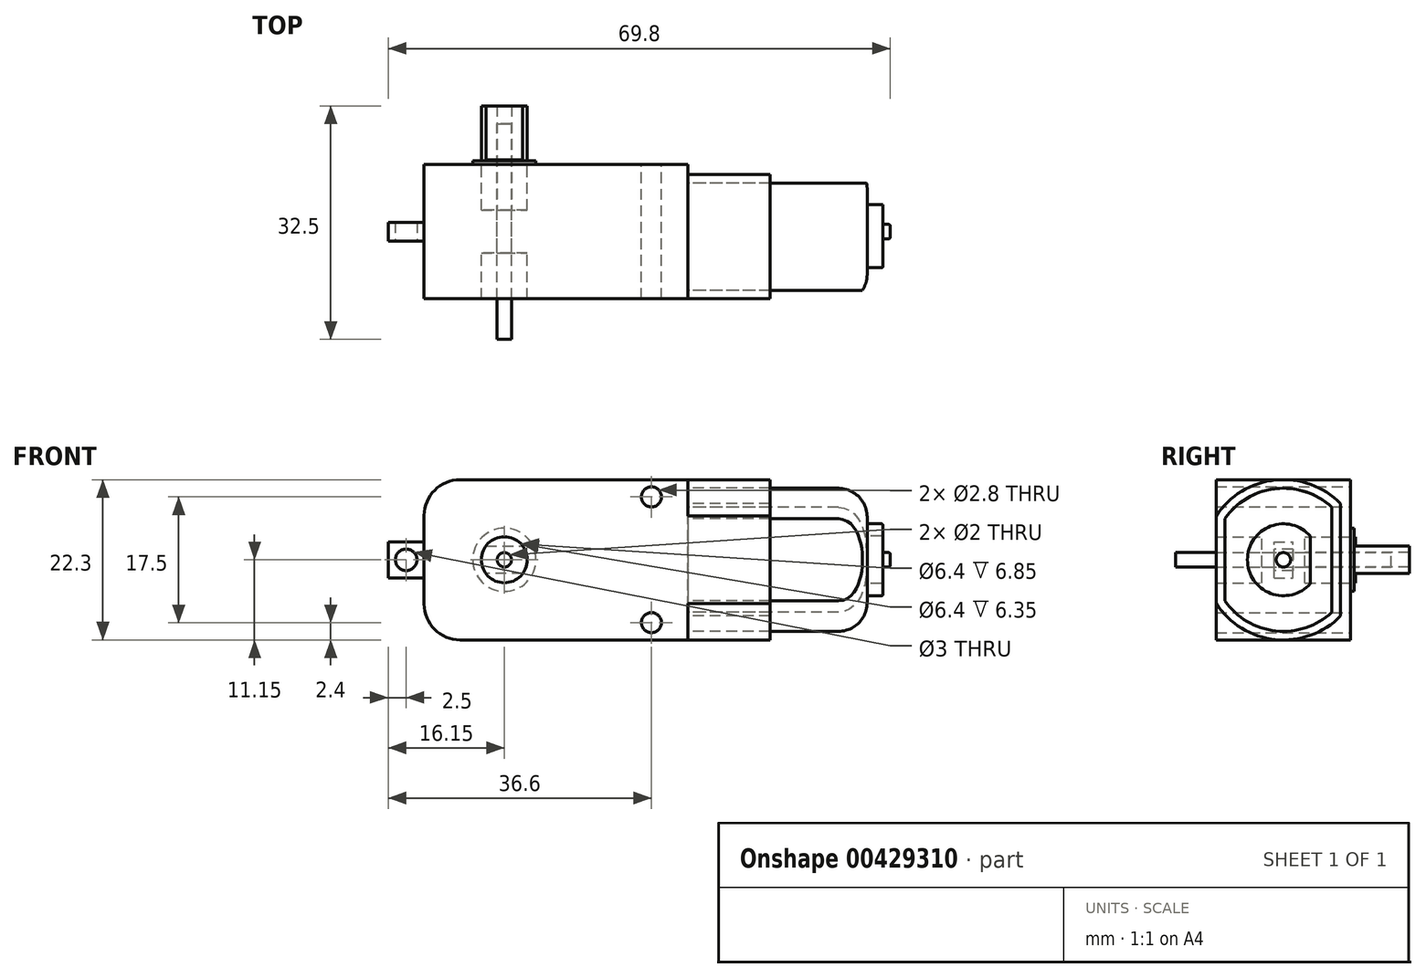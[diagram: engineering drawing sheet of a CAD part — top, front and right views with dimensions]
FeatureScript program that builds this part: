
annotation { "Feature Type Name" : "Feature", "Feature Type Description" : "" }
export const myFeature = defineFeature(function(context is Context, id is Id, definition is map)
    precondition{}
    {
        {
            var Q0;
            Q0=qCreatedBy(makeId("Front.planeOp"),FACE);
            var sketch = newSketch(context, id + "F0", { "sketchPlane" : qUnion([Q0])});
            skLineSegment(sketch, "E0.bottom", {"start": v(18.35, -11.15) * mm, "end": v(-13.35, -11.15) * mm});
            skLineSegment(sketch, "E0.top", {"start": v(18.35, 11.15) * mm, "end": v(-13.35, 11.15) * mm});
            skLineSegment(sketch, "E0.left", {"start": v(18.35, -11.15) * mm, "end": v(18.35, 11.15) * mm});
            skLineSegment(sketch, "E0.right", {"start": v(-18.35, -6.15) * mm, "end": v(-18.35, 6.15) * mm});
            skPoint(sketch, "E0.middle", {"position": v(0, 0) * mm});
            skPoint(sketch, "E1.visualSharp", {"position": v(-18.35, 11.15) * mm});
            skArc(sketch, "E1.filletArc", {"start": v(-13.35, 11.15) * mm, "mid": v(-16.89, 9.69) * mm, "end": v(-18.35, 6.15) * mm});
            skPoint(sketch, "E2.visualSharp", {"position": v(-18.35, -11.15) * mm});
            skArc(sketch, "E2.filletArc", {"start": v(-18.35, -6.15) * mm, "mid": v(-16.89, -9.69) * mm, "end": v(-13.35, -11.15) * mm});
            skLineSegment(sketch, "E3", {"start": v(-27.57, 10.15) * mm, "end": v(27, 10.15) * mm, "construction": true});
            skLineSegment(sketch, "E4", {"start": v(27, -10.15) * mm, "end": v(-33.16, -10.15) * mm, "construction": true});
            skLineSegment(sketch, "E5", {"start": v(14.65, 15.01) * mm, "end": v(14.65, -22.1) * mm, "construction": true});
            skCircle(sketch, "E6", {"center": v(13.25, 8.75) * mm, "radius": 1.4 * mm});
            skCircle(sketch, "E7.MirrorC", {"center": v(13.25, -8.75) * mm, "radius": 1.4 * mm});
            skCircle(sketch, "E8", {"center": v(-7.2, 0) * mm, "radius": 3.2 * mm});
            skCircle(sketch, "E9", {"center": v(-7.2, 0) * mm, "radius": 1 * mm});
            skSolve(sketch);
        }
        {
            var Q0;
            Q0=makeQuery(id+"F0.imprint","IMPRINT",FACE,{"disambiguationData":[TD([[makeQuery(id+"F0.imprint","IMPRINT",EDGE,{"derivedFrom":sQuery(id+"F0.wireOp",EDGE,"E0.bottom")}),-1.0]])]});
            extrude(context, id + "F1", {"entities" : qUnion([Q0]), "endBound" : BoundingType.SYMMETRIC, "depth" : (18.7) * mm});
        }
        {
            var Q0;
            Q0=makeQuery(id+"F1.opExtrude","SWEPT_FACE",FACE,{"disambiguationData":[OSD([sQuery(id+"F0.wireOp",EDGE,"E0.right")])]});
            var sketch = newSketch(context, id + "F2", { "sketchPlane" : qUnion([Q0])});
            skLineSegment(sketch, "E10.bottom", {"start": v(1.3, -2.5) * mm, "end": v(-1.3, -2.5) * mm});
            skLineSegment(sketch, "E10.top", {"start": v(1.3, 2.5) * mm, "end": v(-1.3, 2.5) * mm});
            skLineSegment(sketch, "E10.left", {"start": v(1.3, -2.5) * mm, "end": v(1.3, 2.5) * mm});
            skLineSegment(sketch, "E10.right", {"start": v(-1.3, -2.5) * mm, "end": v(-1.3, 2.5) * mm});
            skPoint(sketch, "E10.middle", {"position": v(0, 0) * mm});
            skSolve(sketch);
        }
        {
            var Q0;
            Q0=makeQuery(id+"F2.imprint","IMPRINT",FACE,{"disambiguationData":[TD([[makeQuery(id+"F2.imprint","IMPRINT",EDGE,{"derivedFrom":sQuery(id+"F2.wireOp",EDGE,"E10.bottom")}),-1.0]])]});
            extrude(context, id + "F3", {"entities" : qUnion([Q0]), "operationType" : NewBodyOperationType.ADD, "depth" : 5 * mm});
        }
        {
            var Q0;
            Q0=makeQuery(id+"F3.opExtrude","SWEPT_FACE",FACE,{"disambiguationData":[OSD([sQuery(id+"F2.wireOp",EDGE,"E10.left")])]});
            var sketch = newSketch(context, id + "F4", { "sketchPlane" : qUnion([Q0])});
            skLineSegment(sketch, "E11", {"start": v(-23.35, 0) * mm, "end": v(-18.35, 0) * mm, "construction": true});
            skCircle(sketch, "E12", {"center": v(-20.85, 0) * mm, "radius": 1.5 * mm});
            skSolve(sketch);
        }
        {
            var Q0;
            Q0=makeQuery(id+"F4.imprint","IMPRINT",FACE,{"disambiguationData":[TD([[makeQuery(id+"F4.imprint","IMPRINT",EDGE,{"derivedFrom":sQuery(id+"F4.wireOp",EDGE,"E12")}),1.0]])]});
            extrude(context, id + "F5", {"entities" : qUnion([Q0]), "operationType" : NewBodyOperationType.REMOVE, "endBound" : BoundingType.THROUGH_ALL, "oppositeDirection" : true, "depth" : 25 * mm});
        }
        {
            var Q0;
            Q0=makeQuery(id+"F1.opExtrude","SWEPT_FACE",FACE,{"disambiguationData":[OSD([sQuery(id+"F0.wireOp",EDGE,"E0.left")])]});
            var sketch = newSketch(context, id + "F6", { "sketchPlane" : qUnion([Q0])});
            skArc(sketch, "E13", {"start": v(7.95, 7.82) * mm, "mid": v(-1.12, 11.1) * mm, "end": v(-9.35, 6.07) * mm});
            skLineSegment(sketch, "E14", {"start": v(7.95, 13.91) * mm, "end": v(7.95, -13.85) * mm, "construction": true});
            skLineSegment(sketch, "E15", {"start": v(-9.35, 11.15) * mm, "end": v(-9.35, -11.15) * mm, "construction": true});
            skArc(sketch, "E16.trimOffspring", {"start": v(-9.35, -6.07) * mm, "mid": v(-1.12, -11.1) * mm, "end": v(7.95, -7.82) * mm});
            skLineSegment(sketch, "E17", {"start": v(-9.35, 6.07) * mm, "end": v(-9.35, -6.07) * mm});
            skLineSegment(sketch, "E18", {"start": v(7.95, 7.82) * mm, "end": v(7.95, -7.82) * mm});
            skArc(sketch, "E19.0", {"start": v(-8.15, -5.7) * mm, "mid": v(-1.06, -9.9) * mm, "end": v(6.75, -7.31) * mm});
            skLineSegment(sketch, "E19.1", {"start": v(-8.15, 5.7) * mm, "end": v(-8.15, -5.7) * mm});
            skArc(sketch, "E19.2", {"start": v(6.75, 7.31) * mm, "mid": v(-1.06, 9.9) * mm, "end": v(-8.15, 5.7) * mm});
            skLineSegment(sketch, "E19.3", {"start": v(6.75, 7.31) * mm, "end": v(6.75, -7.31) * mm});
            skSolve(sketch);
        }
        {
            var Q0;
            {var subQ4=sQuery(id+"F6.wireOp",EDGE,"E17");Q0=makeQuery(id+"F6.imprint","IMPRINT",FACE,{"disambiguationData":[TD([[makeQuery(id+"F6.imprint","IMPRINT",EDGE,{"derivedFrom":subQ4}),-1.0]])]});}
            extrude(context, id + "F7", {"entities" : qUnion([Q0]), "operationType" : NewBodyOperationType.ADD, "depth" : 11.4 * mm});
        }
        {
            var Q0;
            Q0=makeQuery(id+"F7.boolean.opBoolean","SPLIT",FACE,{"disambiguationData":[TD([makeQuery(id+"F7.opExtrude","SWEPT_FACE",FACE,{"disambiguationData":[OSD([sQuery(id+"F6.wireOp",EDGE,"E19.0")])]}),makeQuery(id+"F7.opExtrude","SWEPT_FACE",FACE,{"disambiguationData":[OSD([sQuery(id+"F6.wireOp",EDGE,"E19.1")])]}),makeQuery(id+"F7.opExtrude","SWEPT_FACE",FACE,{"disambiguationData":[OSD([sQuery(id+"F6.wireOp",EDGE,"E19.2")])]}),makeQuery(id+"F7.opExtrude","SWEPT_FACE",FACE,{"disambiguationData":[OSD([sQuery(id+"F6.wireOp",EDGE,"E19.3")])]})])],"derivedFrom":makeQuery(id+"F1.opExtrude","SWEPT_FACE",FACE,{"disambiguationData":[OSD([sQuery(id+"F0.wireOp",EDGE,"E0.left")])]})});
            extrude(context, id + "F8", {"entities" : qUnion([Q0]), "depth" : (11.4 + 13.5) * mm});
        }
        {
            var Q0;
            Q0=makeQuery(id+"F8.opExtrude","CAP_EDGE",EDGE,{"disambiguationData":[OSD([sQuery(id+"F6.wireOp",EDGE,"E19.0")])],"isStart":false});
            fillet(context, id + "F9", {"entities" : qUnion([Q0]), "radius" : 4 * mm, "tangentPropagation" : true, "allowEdgeOverflow" : false});
        }
        {
            var Q0;
            Q0=makeQuery(id+"F8.opExtrude","CAP_FACE",FACE,{"disambiguationData":[OSD([sQuery(id+"F0.wireOp",EDGE,"E0.left")])],"isStart":false});
            var sketch = newSketch(context, id + "F10", { "sketchPlane" : qUnion([Q0])});
            skLineSegment(sketch, "E20", {"start": v(3.75, -5.9) * mm, "end": v(3.75, 7.54) * mm, "construction": true});
            skArc(sketch, "E21", {"start": v(3.75, 3.3) * mm, "mid": v(-5, 0) * mm, "end": v(3.75, -3.3) * mm});
            skLineSegment(sketch, "E22", {"start": v(3.75, 3.3) * mm, "end": v(3.75, -3.3) * mm});
            skCircle(sketch, "E23", {"center": v(0, 0) * mm, "radius": 1 * mm});
            skSolve(sketch);
        }
        {
            var Q0;
            Q0=makeQuery(id+"F0.imprint","IMPRINT",FACE,{"disambiguationData":[TD([[makeQuery(id+"F0.imprint","IMPRINT",EDGE,{"derivedFrom":sQuery(id+"F0.wireOp",EDGE,"E8")}),1.0]])]});
            extrude(context, id + "F11", {"entities" : qUnion([Q0]), "operationType" : NewBodyOperationType.ADD, "endBound" : BoundingType.SYMMETRIC, "depth" : 6 * mm});
        }
        {
            var Q0;
            Q0=makeQuery(id+"F0.imprint","IMPRINT",FACE,{"disambiguationData":[TD([[makeQuery(id+"F0.imprint","IMPRINT",EDGE,{"derivedFrom":sQuery(id+"F0.wireOp",EDGE,"E9")}),1.0]])]});
            extrude(context, id + "F12", {"entities" : qUnion([Q0]), "endBound" : BoundingType.SYMMETRIC, "depth" : 30 * mm});
        }
        {
            var Q0;
            Q0=makeQuery(id+"F1.opExtrude","CAP_FACE",FACE,{"disambiguationData":[OSD([sQuery(id+"F0.wireOp",EDGE,"E0.bottom"),sQuery(id+"F0.wireOp",EDGE,"E0.top"),sQuery(id+"F0.wireOp",EDGE,"E0.left"),sQuery(id+"F0.wireOp",EDGE,"E0.right"),sQuery(id+"F0.wireOp",EDGE,"E1.filletArc"),sQuery(id+"F0.wireOp",EDGE,"E2.filletArc"),sQuery(id+"F0.wireOp",EDGE,"E6"),sQuery(id+"F0.wireOp",EDGE,"E7.MirrorC"),sQuery(id+"F0.wireOp",EDGE,"E8")])],"isStart":true});
            var sketch = newSketch(context, id + "F13", { "sketchPlane" : qUnion([Q0])});
            skCircle(sketch, "E24", {"center": v(7.2, 0) * mm, "radius": 3.2 * mm});
            skCircle(sketch, "E25.0", {"center": v(7.2, 0) * mm, "radius": 4.4 * mm});
            skSolve(sketch);
        }
        {
            var Q0;
            Q0=makeQuery(id+"F13.imprint","IMPRINT",FACE,{"disambiguationData":[TD([[makeQuery(id+"F13.imprint","IMPRINT",EDGE,{"derivedFrom":sQuery(id+"F13.wireOp",EDGE,"E24")}),1.0]])]});
            extrude(context, id + "F14", {"entities" : qUnion([Q0]), "operationType" : NewBodyOperationType.ADD, "depth" : .5 * mm});
        }
        {
            var Q0;
            Q0=makeQuery(id+"F11.opExtrude","CAP_FACE",FACE,{"disambiguationData":[OSD([sQuery(id+"F0.wireOp",EDGE,"E8"),sQuery(id+"F0.wireOp",EDGE,"E9")])],"isStart":true});
            var sketch = newSketch(context, id + "F15", { "sketchPlane" : qUnion([Q0])});
            skCircle(sketch, "E26", {"center": v(7.2, 0) * mm, "radius": 1 * mm});
            skCircle(sketch, "E27", {"center": v(7.2, 0) * mm, "radius": 3.2 * mm});
            skSolve(sketch);
        }
        {
            var Q0;
            Q0=makeQuery(id+"F15.imprint","IMPRINT",FACE,{"disambiguationData":[TD([[makeQuery(id+"F15.imprint","IMPRINT",EDGE,{"derivedFrom":sQuery(id+"F15.wireOp",EDGE,"E26")}),1.0]])]});
            extrude(context, id + "F16", {"entities" : qUnion([Q0]), "depth" : 14.5 * mm});
        }
        {
            var Q0;
            Q0=makeQuery(id+"F16.opExtrude","CAP_FACE",FACE,{"disambiguationData":[OSD([sQuery(id+"F15.wireOp",EDGE,"E26"),sQuery(id+"F15.wireOp",EDGE,"E27")])],"isStart":false});
            var sketch = newSketch(context, id + "F17", { "sketchPlane" : qUnion([Q0])});
            skLineSegment(sketch, "E28", {"start": v(13.52, -1.92) * mm, "end": v(0.5, -1.92) * mm, "construction": true});
            skLineSegment(sketch, "E29", {"start": v(0.5, -1.92) * mm, "end": v(0.83, 1.03) * mm, "construction": true});
            skLineSegment(sketch, "E30.MirrorCS", {"start": v(13.52, 1.92) * mm, "end": v(0.5, 1.92) * mm, "construction": true});
            skLineSegment(sketch, "E31", {"start": v(9.76, 1.92) * mm, "end": v(4.64, 1.92) * mm});
            skLineSegment(sketch, "E32", {"start": v(4.64, -1.92) * mm, "end": v(9.76, -1.92) * mm});
            skSolve(sketch);
        }
        {
            var Q0;
            {var subQ0=sQuery(id+"F17.wireOp",EDGE,"E31");Q0=makeQuery(id+"F17.imprint","IMPRINT",FACE,{"disambiguationData":[TD([[makeQuery(id+"F17.imprint","IMPRINT",EDGE,{"derivedFrom":subQ0}),-1.0]])]});}
            var Q1;
            {var subQ0=sQuery(id+"F17.wireOp",EDGE,"E32");Q1=makeQuery(id+"F17.imprint","IMPRINT",FACE,{"disambiguationData":[TD([[makeQuery(id+"F17.imprint","IMPRINT",EDGE,{"derivedFrom":subQ0}),-1.0]])]});}
            extrude(context, id + "F18", {"entities" : qUnion([Q0, Q1]), "operationType" : NewBodyOperationType.REMOVE, "oppositeDirection" : true, "depth" : 7.5 * mm});
        }
        {
            var Q0;
            Q0=makeQuery(id+"F10.imprint","IMPRINT",FACE,{"disambiguationData":[TD([[makeQuery(id+"F10.imprint","IMPRINT",EDGE,{"derivedFrom":sQuery(id+"F10.wireOp",EDGE,"E21")}),1.0]])]});
            extrude(context, id + "F19", {"entities" : qUnion([Q0]), "operationType" : NewBodyOperationType.ADD, "depth" : 2.2 * mm});
        }
        {
            var Q0;
            Q0=makeQuery(id+"F10.imprint","IMPRINT",FACE,{"disambiguationData":[TD([[makeQuery(id+"F10.imprint","IMPRINT",EDGE,{"derivedFrom":sQuery(id+"F10.wireOp",EDGE,"E23")}),1.0]])]});
            extrude(context, id + "F20", {"entities" : qUnion([Q0]), "operationType" : NewBodyOperationType.ADD, "depth" : 3.2 * mm});
        }
        {
            var Q0;
            Q0=makeQuery(id+"F19.opExtrude","CAP_EDGE",EDGE,{"disambiguationData":[OSD([sQuery(id+"F10.wireOp",EDGE,"E21")])],"isStart":false});
            var Q1;
            Q1=makeQuery(id+"F20.opExtrude","CAP_EDGE",EDGE,{"disambiguationData":[OSD([sQuery(id+"F10.wireOp",EDGE,"E23")])],"isStart":false});
            fillet(context, id + "F21", {"entities" : qUnion([Q0, Q1]), "radius" : .2 * mm, "tangentPropagation" : true, "allowEdgeOverflow" : false});
        }
    });
